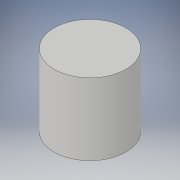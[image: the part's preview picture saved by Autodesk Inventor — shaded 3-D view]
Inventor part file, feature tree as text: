
AUTODESK INVENTOR PART (.ipt)
format: ipt  version: 2018 (Build 220112000, 112)  size: 102,912 bytes
history: native  units: in
note: dims shown in document units (in); Inventor stores cm internally (conversion verified against a paired STEP export)
features: revolve x1, sketch x1
ambient origin geometry x8: Origin, YZ Plane, XZ Plane, XY Plane, X Axis, Y Axis, Z Axis, Center Point
bodies: Solid1 (feature_tree)
feature tree (2):
  revolve  "Revolution1"  [1 undecoded]
  sketch  "Sketch1"  dims[d0=78.7402in d1=39.3701in d2=39.3701in d3=90.0deg]
note: 1 required parameter value undecoded (feature->parameter linkage not recoverable at this tier; creation-order binding heuristic only, values carry confidence <= 0.55)
